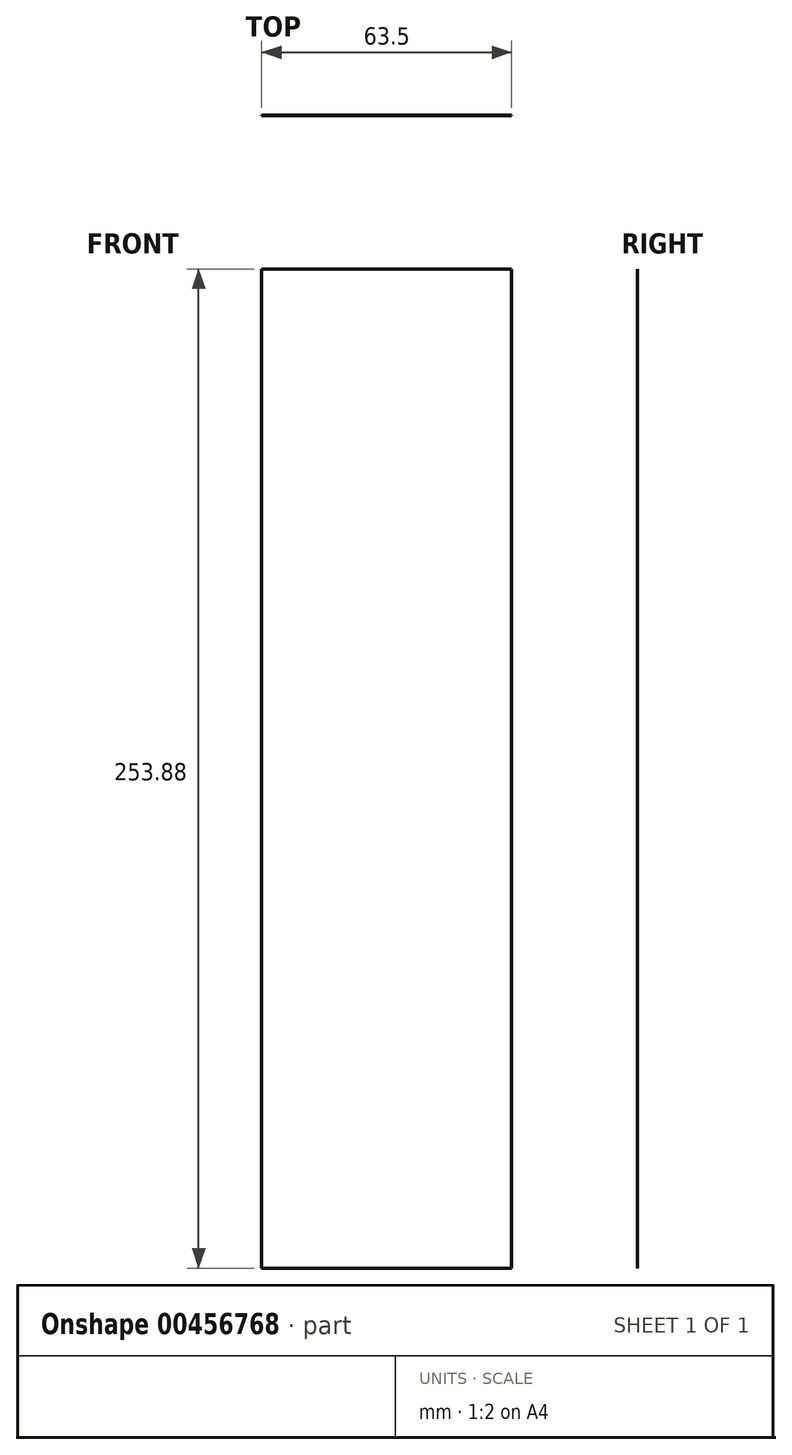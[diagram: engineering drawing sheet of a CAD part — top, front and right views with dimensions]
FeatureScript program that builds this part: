
annotation { "Feature Type Name" : "Feature", "Feature Type Description" : "" }
export const myFeature = defineFeature(function(context is Context, id is Id, definition is map)
    precondition{}
    {
        {
            var Q0;
            Q0=qCreatedBy(makeId("Front.planeOp"),FACE);
            var sketch = newSketch(context, id + "F0", { "sketchPlane" : qUnion([Q0])});
            skLineSegment(sketch, "E0.bottom", {"start": v(-31.75, 126.94) * mm, "end": v(31.75, 126.94) * mm});
            skLineSegment(sketch, "E0.top", {"start": v(-31.75, -126.94) * mm, "end": v(31.75, -126.94) * mm});
            skLineSegment(sketch, "E0.left", {"start": v(-31.75, 126.94) * mm, "end": v(-31.75, -126.94) * mm});
            skLineSegment(sketch, "E0.right", {"start": v(31.75, 126.94) * mm, "end": v(31.75, -126.94) * mm});
            skPoint(sketch, "E0.middle", {"position": v(0, 0) * mm});
            skSolve(sketch);
        }
        {
            var Q0;
            Q0=makeQuery(id+"F0.imprint","IMPRINT",FACE,{"disambiguationData":[TD([[makeQuery(id+"F0.imprint","IMPRINT",EDGE,{"derivedFrom":sQuery(id+"F0.wireOp",EDGE,"E0.bottom")}),-1.0]])]});
            extrude(context, id + "F1", {"entities" : qUnion([Q0]), "depth" : 1 / 203.2 * mm});
        }
    });
